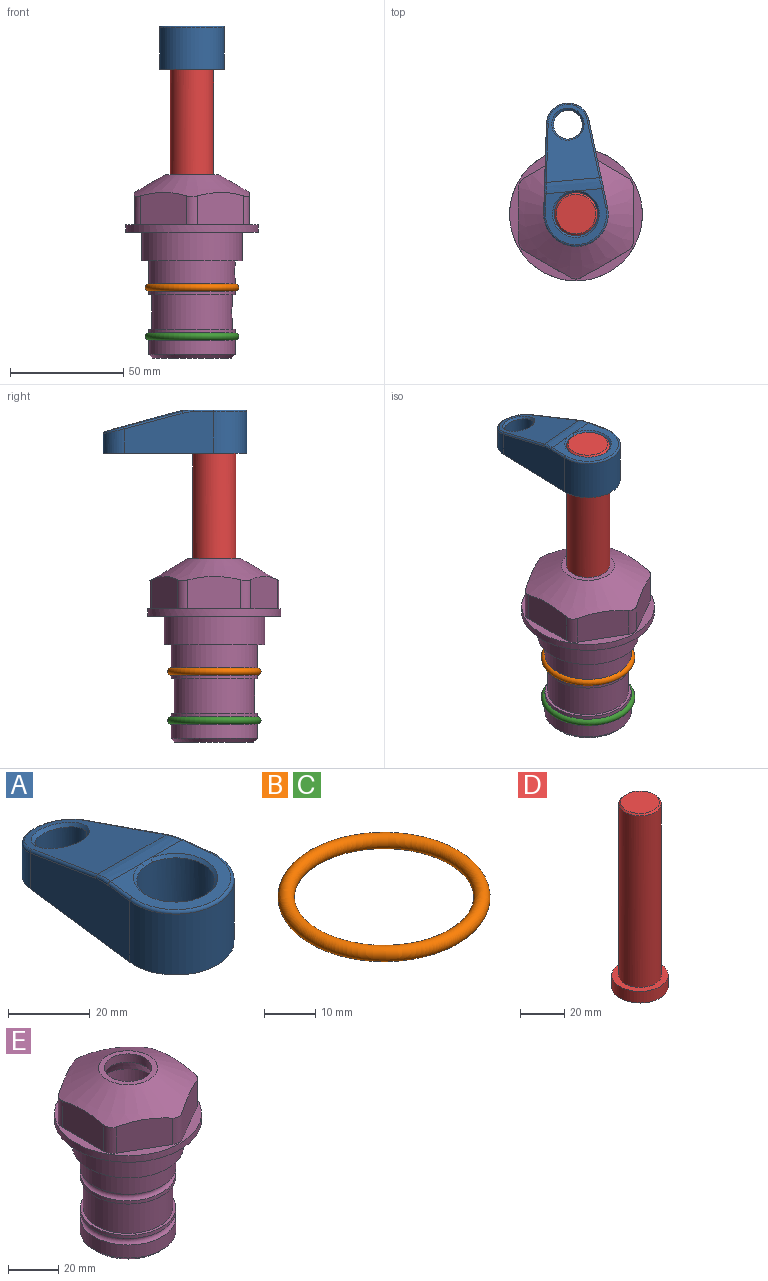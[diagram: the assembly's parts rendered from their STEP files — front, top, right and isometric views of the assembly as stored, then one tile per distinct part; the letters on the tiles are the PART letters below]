
ASSEMBLY  parts=5 mates=4
PART A: 31 faces, bbox 31.7x65.5x19.8 mm
  f0: plane 39.12x18.26mm, normal (0.99,0.12,0), area 612.2mm2, adj f1,f4,f7,f11,f13,f15
  f1: cylinder r=9.53mm len=18.91mm, axis (0,0,-1), area 296.1mm2, adj f0,f2,f7,f17
  f2: plane 39.12x18.26mm, normal (-0.99,0.12,0), area 612.2mm2, adj f1,f4,f7,f12,f14,f16
  f3: cylinder r=6.35mm len=12.7mm, axis (0,0,-1), area 362.4mm2, adj f7,f18
  f4: cylinder r=14.29mm len=28.58mm, axis (0,0,-1), area 882.2mm2, adj f0,f2,f7,f10
  f5: cylinder r=9.53mm len=19.05mm, axis (0,0,-1), area 1092.6mm2, adj f7,f19,f20
  f6: plane 26.99x23.69mm, normal (0,0,1), area 216.2mm2, adj f9,f10,f11,f12,f19
  f7: plane 63.5x28.58mm, normal (0,0,-1), area 661.8mm2, adj f0,f1,f2,f3,f4,f5,f22,f23
  f8: plane 33.52x23.6mm, normal (0,0.26,0.97), area 486mm2, adj f9,f15,f16,f17,f18
  f9: cylinder r=19.05mm len=24.72mm, axis (1,0,0), area 120.4mm2, adj f6,f8,f13,f14,f20
  f10: torus R=13.49mm, axis (0,0,1), area 59mm2, adj f4,f6,f11,f12
  f11: cylinder r=0.79mm len=8.67mm, axis (0.12,-0.99,0), area 10.8mm2, adj f0,f6,f10,f13
  f12: cylinder r=0.79mm len=8.67mm, axis (0.12,0.99,0), area 10.8mm2, adj f2,f6,f10,f14
  f13: bspline ~4.95x1.42mm, area 6.1mm2, adj f0,f9,f11,f15
  f14: bspline ~4.95x1.42mm, area 6.1mm2, adj f2,f9,f12,f16
  f15: cylinder r=0.79mm len=25.95mm, axis (0.12,-0.96,0.26), area 32.9mm2, adj f0,f8,f13,f17
  f16: cylinder r=0.79mm len=25.95mm, axis (0.12,0.96,-0.26), area 32.9mm2, adj f2,f8,f14,f17
  f17: bspline ~18.91x8.38mm, area 30mm2, adj f1,f8,f15,f16
  f18: bspline ~14.29x14.29mm, area 48.3mm2, adj f3,f8
  f19: cone r=9.53mm half-angle=45deg, axis (0,0,1), area 66.5mm2, adj f5,f6,f20
  f20: bspline ~3.22x0.96mm, area 3.5mm2, adj f5,f9,f19
  f21: plane 2.75x2.72mm, normal (0,0,-1), area 2.9mm2, adj f23,f25,f28
  f22: plane 23.05x15.88mm, normal (-0.99,-0.12,0), area 323.6mm2, adj f7,f25,f26,f27,f28,f29
  f23: plane 23.05x15.88mm, normal (0.99,-0.12,0), area 323.6mm2, adj f7,f21,f25,f27,f28,f30
  f24: cylinder r=9.53mm len=10.69mm, axis (0,0,-1), area 114.7mm2, adj f7,f27,f29,f30
  f25: cylinder r=12.7mm len=20.59mm, axis (0,0,-1), area 381.1mm2, adj f7,f21,f22,f23,f26,f28
  f26: plane 2.75x2.72mm, normal (0,0,-1), area 2.9mm2, adj f22,f25,f28
  f27: plane 19.72x18.37mm, normal (0,-0.26,-0.97), area 291.8mm2, adj f22,f23,f24,f28,f29,f30
  f28: cylinder r=15.88mm len=19.92mm, axis (1,0,0), area 54.8mm2, adj f21,f22,f23,f25,f26,f27
  f29: cylinder r=1.59mm len=11mm, axis (0,0,-1), area 34.7mm2, adj f7,f22,f24,f27
  f30: cylinder r=1.59mm len=11mm, axis (0,0,-1), area 34.7mm2, adj f7,f23,f24,f27
PART B: 1 faces, bbox 44.7x44.7x3.2 mm
  f0: torus R=19.05mm, axis (0,0,1), area 1193.9mm2
PART C: same geometry as B
PART D: 6 faces, bbox 25.4x25.4x101.6 mm
  f0: plane 17.46x17.46mm, normal (0,0,1), area 239.5mm2, adj f5
  f1: plane 25.4x25.4mm, normal (0,0,-1), area 506.7mm2, adj f2
  f2: cylinder r=12.7mm len=25.4mm, axis (0,0,1), area 506.7mm2, adj f1,f3
  f3: plane 25.4x25.4mm, normal (0,0,1), area 221.7mm2, adj f2,f4
  f4: cylinder r=9.53mm len=94.46mm, axis (0,0,1), area 5653mm2, adj f3,f5
  f5: cone r=8.73mm half-angle=45deg, axis (0,0,-1), area 64.4mm2, adj f0,f4
PART E: 36 faces, bbox 58.7x58.7x81 mm
  f0: cylinder r=17.78mm len=35.56mm, axis (0,0,1), area 1670.8mm2, adj f23,f24,f31
  f1: cylinder r=19.05mm len=38.1mm, axis (0,0,1), area 1191.9mm2, adj f26,f27,f30
  f2: plane 58.66x58.66mm, normal (0,0,-1), area 1150.6mm2, adj f3,f28
  f3: cylinder r=29.33mm len=58.66mm, axis (0,0,-1), area 585.1mm2, adj f2,f4
  f4: plane 58.66x58.66mm, normal (0,0,1), area 475.9mm2, adj f3,f5,f6,f7,f8,f9,f10,f11
  f5: plane 20.32x14.34mm, normal (-0.5,0.87,0), area 324.4mm2, adj f4,f15,f16,f17
  f6: plane 20.32x14.34mm, normal (0.5,0.87,0), area 324.4mm2, adj f4,f14,f15,f17
  f7: plane 23.48x14.34mm, normal (1,0,0), area 324.4mm2, adj f4,f13,f14,f17
  f8: plane 20.32x14.34mm, normal (0.5,-0.87,0), area 324.4mm2, adj f4,f12,f13,f17
  f9: plane 20.32x14.34mm, normal (-0.5,-0.87,0), area 324.4mm2, adj f4,f11,f12,f17
  f10: plane 23.48x14.34mm, normal (-1,0,0), area 324.4mm2, adj f4,f11,f16,f17
  f11: cylinder r=5.08mm len=12.85mm, axis (0,0,-1), area 67.2mm2, adj f4,f9,f10,f17
  f12: cylinder r=5.08mm len=12.85mm, axis (0,0,-1), area 67.2mm2, adj f4,f8,f9,f17
  f13: cylinder r=5.08mm len=12.85mm, axis (0,0,-1), area 67.2mm2, adj f4,f7,f8,f17
  f14: cylinder r=5.08mm len=12.85mm, axis (0,0,-1), area 67.2mm2, adj f4,f6,f7,f17
  f15: cylinder r=5.08mm len=12.85mm, axis (0,0,-1), area 67.2mm2, adj f4,f5,f6,f17
  f16: cylinder r=5.08mm len=12.85mm, axis (0,0,-1), area 67.2mm2, adj f4,f5,f10,f17
  f17: cone r=11.73mm half-angle=60deg, axis (0,0,-1), area 2071.8mm2, adj f5,f6,f7,f8,f9,f10,f11,f12
  f18: plane 23.46x23.46mm, normal (0,0,1), area 147.4mm2, adj f17,f35
  f19: plane 34.93x34.93mm, normal (0,0,-1), area 958mm2, adj f29
  f20: cylinder r=19.05mm len=38.1mm, axis (0,0,1), area 760.1mm2, adj f21,f29
  f21: torus R=19.05mm, axis (0,0,1), area 565.3mm2, adj f20,f22
  f22: cylinder r=19.05mm len=38.1mm, axis (0,0,1), area 190mm2, adj f21,f23
  f23: plane 38.1x38.1mm, normal (0,0,1), area 146.9mm2, adj f0,f22
  f24: plane 38.1x38.1mm, normal (0,0,-1), area 146.9mm2, adj f0,f25
  f25: cylinder r=19.05mm len=38.1mm, axis (0,0,1), area 190mm2, adj f24,f26
  f26: torus R=19.05mm, axis (0,0,1), area 565.3mm2, adj f1,f25
  f27: plane 44.45x44.45mm, normal (0,0,-1), area 411.7mm2, adj f1,f28
  f28: cylinder r=22.23mm len=44.45mm, axis (0,0,1), area 1773.5mm2, adj f2,f27
  f29: cone r=19.05mm half-angle=45deg, axis (0,0,1), area 257.5mm2, adj f19,f20
  f30: cylinder r=3.17mm len=6.75mm, axis (-1,0,0), area 128mm2, adj f1,f33
  f31: cylinder r=3.17mm len=6.35mm, axis (-1,0,0), area 102.5mm2, adj f0,f33
  f32: plane 25.4x25.4mm, normal (0,0,1), area 506.7mm2, adj f33
  f33: cylinder r=12.7mm len=66.42mm, axis (0,0,-1), area 5236.2mm2, adj f30,f31,f32,f34
  f34: cone r=9.53mm half-angle=30deg, axis (0,0,-1), area 443.4mm2, adj f33,f35
  f35: cylinder r=9.53mm len=19.05mm, axis (0,0,-1), area 240.9mm2, adj f18,f34
PLACE A rot(axis=(0,0,1),5.1deg) t=(0,0,27.55)mm
PLACE B at identity
PLACE C t=(0,0,-21.59)mm
PLACE D rot(axis=(0,0,1),5.1deg) t=(0,0,27.55)mm
PLACE E at identity fixed
MATE fastened A.f4 <-> D.f2  axis (0,0,-1) through (0,0,90.26)mm
MATE fastened E.f0 <-> B.f0  axis (0,0,1) through (0,0,-24.51)mm
MATE fastened E.f0 <-> C.f0  axis (0,0,1) through (0,0,-46.1)mm
MATE cylindrical E.f0 <-> D.f2  axis (0,0,1) through (0,0,-50.55)mm
